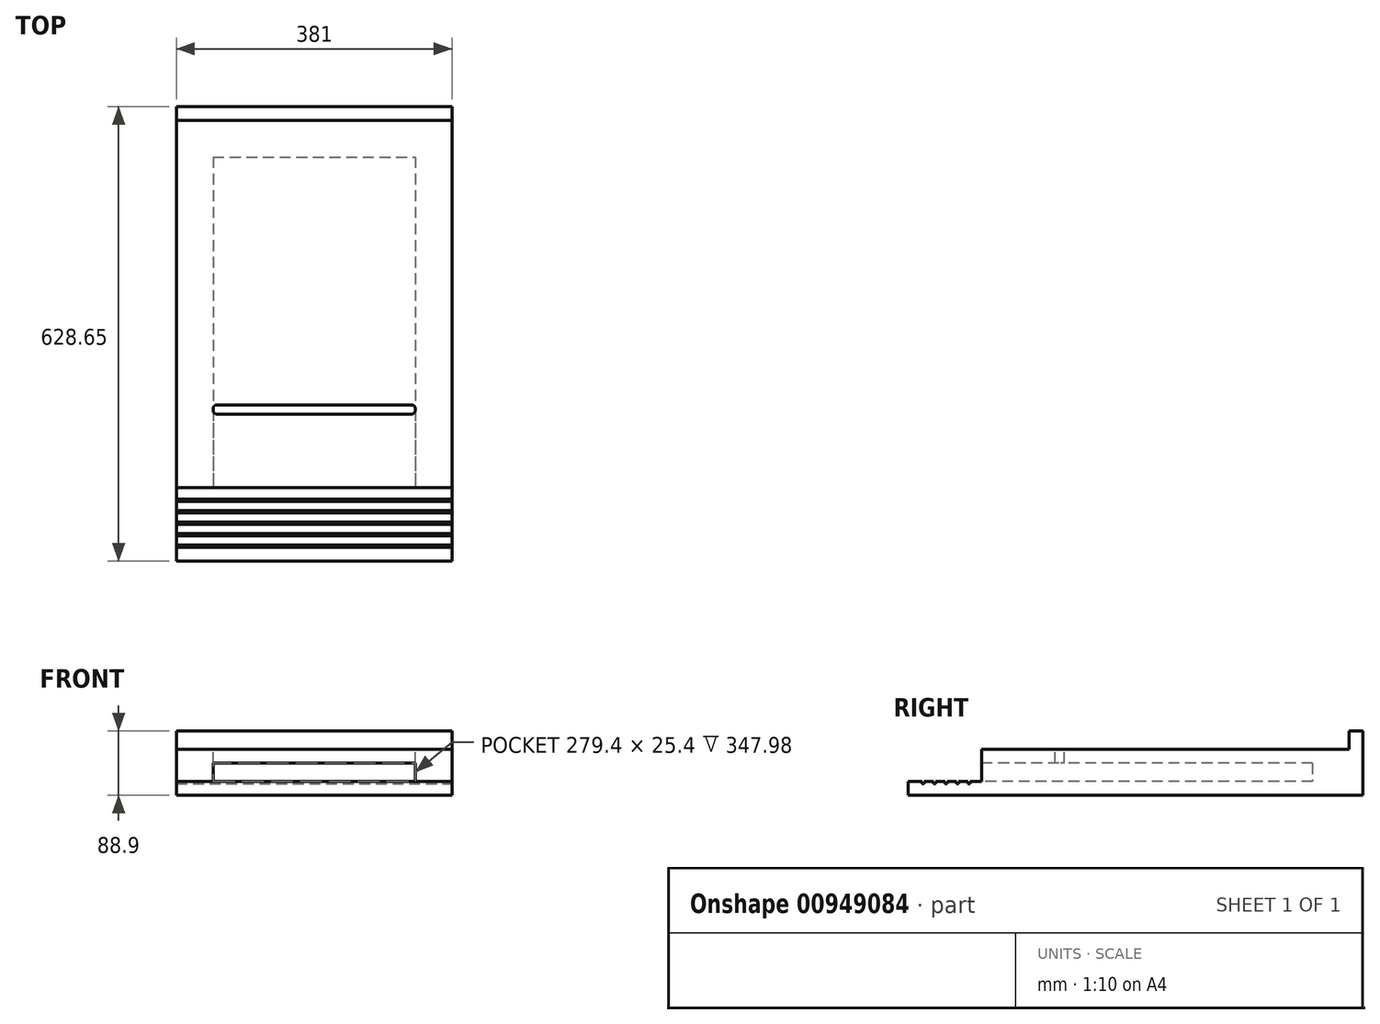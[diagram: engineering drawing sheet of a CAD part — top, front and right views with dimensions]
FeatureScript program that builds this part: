
annotation { "Feature Type Name" : "Feature", "Feature Type Description" : "" }
export const myFeature = defineFeature(function(context is Context, id is Id, definition is map)
    precondition{}
    {
        {
            var Q0;
            Q0=qCreatedBy(makeId("Top.planeOp"),FACE);
            var sketch = newSketch(context, id + "F0", { "sketchPlane" : qUnion([Q0])});
            skLineSegment(sketch, "E0.bottom", {"start": v(0, 0) * mm, "end": v(-381, 0) * mm});
            skLineSegment(sketch, "E0.top", {"start": v(0, 609.6) * mm, "end": v(-381, 609.6) * mm});
            skLineSegment(sketch, "E0.left", {"start": v(0, 0) * mm, "end": v(0, 609.6) * mm});
            skLineSegment(sketch, "E0.right", {"start": v(-381, 0) * mm, "end": v(-381, 609.6) * mm});
            skSolve(sketch);
        }
        {
            var Q0;
            Q0 = qSketchRegion(id + "F0", true);
            extrude(context, id + "F1", {"entities" : qUnion([Q0]), "depth" : 19.05 * mm, "offsetDistance" : 25.4 * mm});
        }
        {
            var Q0;
            Q0=makeQuery(id+"F1.opExtrude","CAP_FACE",FACE,{"disambiguationData":[OSD([sQuery(id+"F0.wireOp",EDGE,"E0.bottom"),sQuery(id+"F0.wireOp",EDGE,"E0.top"),sQuery(id+"F0.wireOp",EDGE,"E0.left"),sQuery(id+"F0.wireOp",EDGE,"E0.right")])],"isStart":false});
            var sketch = newSketch(context, id + "F2", { "sketchPlane" : qUnion([Q0])});
            skLineSegment(sketch, "E1.bottom", {"start": v(-381, 609.6) * mm, "end": v(0, 609.6) * mm});
            skLineSegment(sketch, "E1.top", {"start": v(-381, 558.8) * mm, "end": v(0, 558.8) * mm});
            skLineSegment(sketch, "E1.left", {"start": v(-381, 609.6) * mm, "end": v(-381, 558.8) * mm});
            skLineSegment(sketch, "E1.right", {"start": v(0, 609.6) * mm, "end": v(0, 558.8) * mm});
            skLineSegment(sketch, "E2.bottom", {"start": v(-381, 558.8) * mm, "end": v(-330.2, 558.8) * mm});
            skLineSegment(sketch, "E2.top", {"start": v(-381, 101.6) * mm, "end": v(-330.2, 101.6) * mm});
            skLineSegment(sketch, "E2.left", {"start": v(-381, 558.8) * mm, "end": v(-381, 101.6) * mm});
            skLineSegment(sketch, "E2.right", {"start": v(-330.2, 558.8) * mm, "end": v(-330.2, 101.6) * mm});
            skLineSegment(sketch, "E3.bottom", {"start": v(0, 558.8) * mm, "end": v(-50.8, 558.8) * mm});
            skLineSegment(sketch, "E3.top", {"start": v(0, 101.6) * mm, "end": v(-50.8, 101.6) * mm});
            skLineSegment(sketch, "E3.left", {"start": v(0, 558.8) * mm, "end": v(0, 101.6) * mm});
            skLineSegment(sketch, "E3.right", {"start": v(-50.8, 558.8) * mm, "end": v(-50.8, 101.6) * mm});
            skSolve(sketch);
        }
        {
            var Q0;
            Q0=makeQuery(id+"F2.imprint","IMPRINT",FACE,{"disambiguationData":[TD([[makeQuery(id+"F2.imprint","IMPRINT",EDGE,{"derivedFrom":sQuery(id+"F2.wireOp",EDGE,"E3.top")}),-1.0]])]});
            var Q1;
            Q1=makeQuery(id+"F2.imprint","IMPRINT",FACE,{"disambiguationData":[TD([[makeQuery(id+"F2.imprint","IMPRINT",EDGE,{"derivedFrom":sQuery(id+"F2.wireOp",EDGE,"E1.bottom")}),1.0]])]});
            var Q2;
            Q2=makeQuery(id+"F2.imprint","IMPRINT",FACE,{"disambiguationData":[TD([[makeQuery(id+"F2.imprint","IMPRINT",EDGE,{"derivedFrom":sQuery(id+"F2.wireOp",EDGE,"E2.top")}),1.0]])]});
            extrude(context, id + "F3", {"entities" : qUnion([Q0, Q1, Q2]), "operationType" : NewBodyOperationType.ADD, "depth" : 25.4 * mm, "offsetDistance" : 25.4 * mm});
        }
        {
            var Q0;
            Q0=makeQuery(id+"F3.opExtrude","CAP_FACE",FACE,{"disambiguationData":[OSD([sQuery(id+"F2.wireOp",EDGE,"E1.bottom"),sQuery(id+"F2.wireOp",EDGE,"E1.top"),sQuery(id+"F2.wireOp",EDGE,"E1.left"),sQuery(id+"F2.wireOp",EDGE,"E1.right"),sQuery(id+"F2.wireOp",EDGE,"E2.top"),sQuery(id+"F2.wireOp",EDGE,"E2.left"),sQuery(id+"F2.wireOp",EDGE,"E2.right"),sQuery(id+"F2.wireOp",EDGE,"E3.top"),sQuery(id+"F2.wireOp",EDGE,"E3.left"),sQuery(id+"F2.wireOp",EDGE,"E3.right")])],"isStart":false});
            var sketch = newSketch(context, id + "F4", { "sketchPlane" : qUnion([Q0])});
            skLineSegment(sketch, "E4.bottom", {"start": v(-381, 609.6) * mm, "end": v(0, 609.6) * mm});
            skLineSegment(sketch, "E4.top", {"start": v(-381, 101.6) * mm, "end": v(0, 101.6) * mm});
            skLineSegment(sketch, "E4.left", {"start": v(-381, 609.6) * mm, "end": v(-381, 101.6) * mm});
            skLineSegment(sketch, "E4.right", {"start": v(0, 609.6) * mm, "end": v(0, 101.6) * mm});
            skSolve(sketch);
        }
        {
            var Q0;
            Q0 = qSketchRegion(id + "F4", true);
            extrude(context, id + "F5", {"entities" : qUnion([Q0]), "operationType" : NewBodyOperationType.ADD, "depth" : 19.05 * mm, "offsetDistance" : 25.4 * mm});
        }
        {
            var Q0;
            Q0=makeQuery(id+"F5.boolean.opBoolean","MERGE",FACE,{"derivedFrom":[makeQuery(id+"F3.boolean.opBoolean","MERGE",FACE,{"derivedFrom":[makeQuery(id+"F1.opExtrude","SWEPT_FACE",FACE,{"disambiguationData":[OSD([sQuery(id+"F0.wireOp",EDGE,"E0.top")])]}),makeQuery(id+"F3.opExtrude","SWEPT_FACE",FACE,{"disambiguationData":[OSD([sQuery(id+"F2.wireOp",EDGE,"E1.bottom")])]})]}),makeQuery(id+"F5.opExtrude","SWEPT_FACE",FACE,{"disambiguationData":[OSD([sQuery(id+"F4.wireOp",EDGE,"E4.bottom")])]})]});
            var sketch = newSketch(context, id + "F6", { "sketchPlane" : qUnion([Q0])});
            skLineSegment(sketch, "E5.bottom", {"start": v(0, 0) * mm, "end": v(381, 0) * mm});
            skLineSegment(sketch, "E5.top", {"start": v(0, 88.9) * mm, "end": v(381, 88.9) * mm});
            skLineSegment(sketch, "E5.left", {"start": v(0, 0) * mm, "end": v(0, 88.9) * mm});
            skLineSegment(sketch, "E5.right", {"start": v(381, 0) * mm, "end": v(381, 88.9) * mm});
            skSolve(sketch);
        }
        {
            var Q0;
            Q0 = qSketchRegion(id + "F6", true);
            extrude(context, id + "F7", {"entities" : qUnion([Q0]), "operationType" : NewBodyOperationType.ADD, "depth" : 19.05 * mm, "offsetDistance" : 25.4 * mm});
        }
        {
            var Q0;
            Q0=makeQuery(id+"F7.boolean.opBoolean","MERGE",FACE,{"derivedFrom":[makeQuery(id+"F5.boolean.opBoolean","MERGE",FACE,{"derivedFrom":[makeQuery(id+"F3.boolean.opBoolean","MERGE",FACE,{"derivedFrom":[makeQuery(id+"F1.opExtrude","SWEPT_FACE",FACE,{"disambiguationData":[OSD([sQuery(id+"F0.wireOp",EDGE,"E0.left")])]}),makeQuery(id+"F3.opExtrude","SWEPT_FACE",FACE,{"disambiguationData":[OSD([sQuery(id+"F2.wireOp",EDGE,"E1.right"),sQuery(id+"F2.wireOp",EDGE,"E3.left")])]})]}),makeQuery(id+"F5.opExtrude","SWEPT_FACE",FACE,{"disambiguationData":[OSD([sQuery(id+"F4.wireOp",EDGE,"E4.right")])]})]}),makeQuery(id+"F7.opExtrude","SWEPT_FACE",FACE,{"disambiguationData":[OSD([sQuery(id+"F6.wireOp",EDGE,"E5.left")])]})]});
            var sketch = newSketch(context, id + "F8", { "sketchPlane" : qUnion([Q0])});
            skLineSegment(sketch, "E6.bottom", {"start": v(19.05, 19.05) * mm, "end": v(22.22, 19.05) * mm});
            skLineSegment(sketch, "E6.top", {"start": v(19.05, 15.87) * mm, "end": v(22.22, 15.87) * mm});
            skLineSegment(sketch, "E6.left", {"start": v(19.05, 19.05) * mm, "end": v(19.05, 15.87) * mm});
            skLineSegment(sketch, "E6.right", {"start": v(22.22, 19.05) * mm, "end": v(22.22, 15.87) * mm});
            skLineSegment(sketch, "E7.bottom", {"start": v(34.92, 19.05) * mm, "end": v(38.1, 19.05) * mm});
            skLineSegment(sketch, "E7.top", {"start": v(34.92, 15.87) * mm, "end": v(38.1, 15.87) * mm});
            skLineSegment(sketch, "E7.left", {"start": v(34.92, 19.05) * mm, "end": v(34.92, 15.87) * mm});
            skLineSegment(sketch, "E7.right", {"start": v(38.1, 19.05) * mm, "end": v(38.1, 15.87) * mm});
            skLineSegment(sketch, "E8.bottom", {"start": v(50.8, 19.05) * mm, "end": v(53.97, 19.05) * mm});
            skLineSegment(sketch, "E8.top", {"start": v(50.8, 15.87) * mm, "end": v(53.97, 15.87) * mm});
            skLineSegment(sketch, "E8.left", {"start": v(50.8, 19.05) * mm, "end": v(50.8, 15.87) * mm});
            skLineSegment(sketch, "E8.right", {"start": v(53.97, 19.05) * mm, "end": v(53.97, 15.87) * mm});
            skLineSegment(sketch, "E9.bottom", {"start": v(66.67, 19.05) * mm, "end": v(69.85, 19.05) * mm});
            skLineSegment(sketch, "E9.top", {"start": v(66.67, 15.88) * mm, "end": v(69.85, 15.88) * mm});
            skLineSegment(sketch, "E9.left", {"start": v(66.67, 19.05) * mm, "end": v(66.67, 15.88) * mm});
            skLineSegment(sketch, "E9.right", {"start": v(69.85, 19.05) * mm, "end": v(69.85, 15.87) * mm});
            skLineSegment(sketch, "E10.bottom", {"start": v(82.55, 19.05) * mm, "end": v(85.72, 19.05) * mm});
            skLineSegment(sketch, "E10.top", {"start": v(82.55, 15.88) * mm, "end": v(85.72, 15.88) * mm});
            skLineSegment(sketch, "E10.left", {"start": v(82.55, 19.05) * mm, "end": v(82.55, 15.88) * mm});
            skLineSegment(sketch, "E10.right", {"start": v(85.72, 19.05) * mm, "end": v(85.72, 15.88) * mm});
            skSolve(sketch);
        }
        {
            var Q0;
            Q0 = qSketchRegion(id + "F8", true);
            extrude(context, id + "F9", {"entities" : qUnion([Q0]), "operationType" : NewBodyOperationType.REMOVE, "oppositeDirection" : true, "depth" : 381 * mm, "offsetDistance" : 25.4 * mm});
        }
        {
            var Q0;
            Q0=makeQuery(id+"F5.opExtrude","CAP_FACE",FACE,{"disambiguationData":[OSD([sQuery(id+"F4.wireOp",EDGE,"E4.bottom"),sQuery(id+"F4.wireOp",EDGE,"E4.top"),sQuery(id+"F4.wireOp",EDGE,"E4.left"),sQuery(id+"F4.wireOp",EDGE,"E4.right")])],"isStart":false});
            var sketch = newSketch(context, id + "F10", { "sketchPlane" : qUnion([Q0])});
            skLineSegment(sketch, "E11.bottom", {"start": v(-330.2, 215.9) * mm, "end": v(-50.8, 215.9) * mm});
            skLineSegment(sketch, "E11.top", {"start": v(-330.2, 203.2) * mm, "end": v(-50.8, 203.2) * mm});
            skLineSegment(sketch, "E11.left", {"start": v(-330.2, 215.9) * mm, "end": v(-330.2, 203.2) * mm});
            skLineSegment(sketch, "E11.right", {"start": v(-50.8, 215.9) * mm, "end": v(-50.8, 203.2) * mm});
            skSolve(sketch);
        }
        {
            var Q0;
            Q0 = qSketchRegion(id + "F10", true);
            extrude(context, id + "F11", {"entities" : qUnion([Q0]), "operationType" : NewBodyOperationType.REMOVE, "oppositeDirection" : true, "depth" : 19.05 * mm, "offsetDistance" : 25.4 * mm});
        }
        {
            var Q0;
            Q0=makeQuery(id+"F11.boolean.opBoolean","COPY",EDGE,{"derivedFrom":makeQuery(id+"F11.opExtrude","SWEPT_EDGE",EDGE,{"disambiguationData":[OSD([sQuery(id+"F10.wireOp",EDGE,"E11.bottom"),sQuery(id+"F10.wireOp",EDGE,"E11.left")])]})});
            var Q1;
            Q1=makeQuery(id+"F11.boolean.opBoolean","COPY",EDGE,{"derivedFrom":makeQuery(id+"F11.opExtrude","SWEPT_EDGE",EDGE,{"disambiguationData":[OSD([sQuery(id+"F10.wireOp",EDGE,"E11.top"),sQuery(id+"F10.wireOp",EDGE,"E11.left")])]})});
            var Q2;
            Q2=makeQuery(id+"F11.boolean.opBoolean","COPY",EDGE,{"derivedFrom":makeQuery(id+"F11.opExtrude","SWEPT_EDGE",EDGE,{"disambiguationData":[OSD([sQuery(id+"F10.wireOp",EDGE,"E11.bottom"),sQuery(id+"F10.wireOp",EDGE,"E11.right")])]})});
            var Q3;
            Q3=makeQuery(id+"F11.boolean.opBoolean","COPY",EDGE,{"derivedFrom":makeQuery(id+"F11.opExtrude","SWEPT_EDGE",EDGE,{"disambiguationData":[OSD([sQuery(id+"F10.wireOp",EDGE,"E11.top"),sQuery(id+"F10.wireOp",EDGE,"E11.right")])]})});
            fillet(context, id + "F12", {"entities" : qUnion([Q0, Q1, Q2, Q3]), "radius" : 5.08 * mm, "tangentPropagation" : true, "allowEdgeOverflow" : false});
        }
    });
